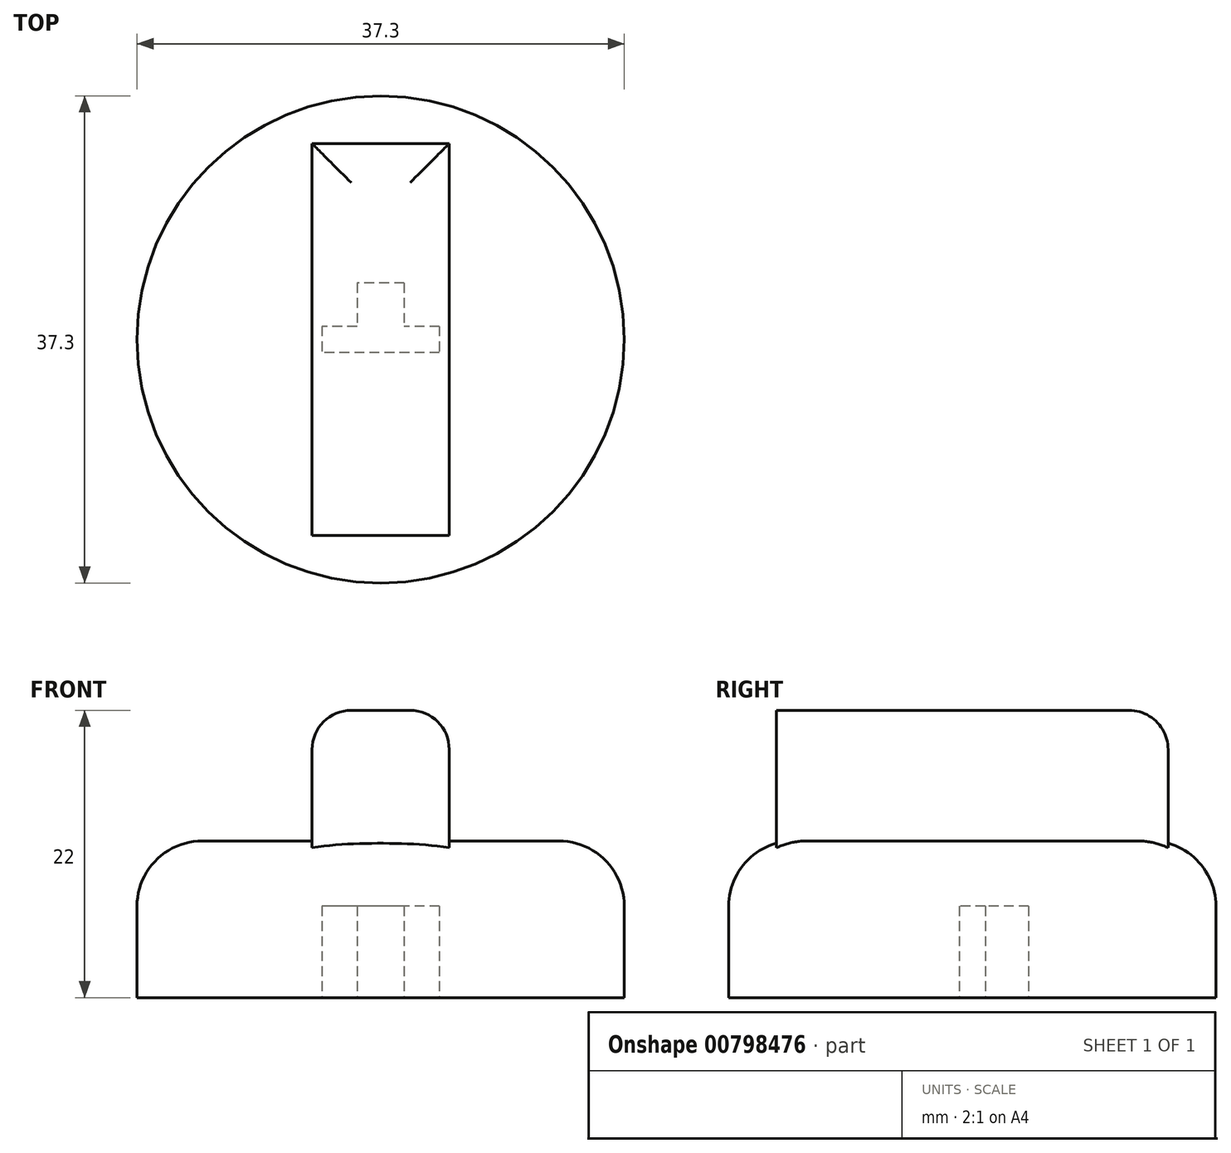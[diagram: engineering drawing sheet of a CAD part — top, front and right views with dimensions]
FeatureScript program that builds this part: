
annotation { "Feature Type Name" : "Feature", "Feature Type Description" : "" }
export const myFeature = defineFeature(function(context is Context, id is Id, definition is map)
    precondition{}
    {
        {
            var Q0;
            Q0=qCreatedBy(makeId("Top.planeOp"),FACE);
            var sketch = newSketch(context, id + "F0", { "sketchPlane" : qUnion([Q0])});
            skLineSegment(sketch, "E0.bottom", {"start": v(4.5, 1) * mm, "end": v(-4.5, 1) * mm});
            skLineSegment(sketch, "E0.top", {"start": v(4.5, -1) * mm, "end": v(-4.5, -1) * mm});
            skLineSegment(sketch, "E0.left", {"start": v(4.5, 1) * mm, "end": v(4.5, -1) * mm});
            skLineSegment(sketch, "E0.right", {"start": v(-4.5, 1) * mm, "end": v(-4.5, -1) * mm});
            skPoint(sketch, "E0.middle", {"position": v(0, 0) * mm});
            skLineSegment(sketch, "E1.bottom", {"start": v(1.8, 4.32) * mm, "end": v(-1.8, 4.32) * mm});
            skLineSegment(sketch, "E1.top", {"start": v(1.8, -1) * mm, "end": v(-1.8, -1) * mm});
            skLineSegment(sketch, "E1.left", {"start": v(1.8, 4.32) * mm, "end": v(1.8, -1) * mm});
            skLineSegment(sketch, "E1.right", {"start": v(-1.8, 4.32) * mm, "end": v(-1.8, -1) * mm});
            skPoint(sketch, "E1.middle", {"position": v(0, 1.66) * mm});
            skCircle(sketch, "E2", {"center": v(0, 0) * mm, "radius": 7 * mm});
            skCircle(sketch, "E3", {"center": v(0, 0) * mm, "radius": 18.65 * mm});
            skSolve(sketch);
        }
        {
            var Q0;
            {var subQ6=sQuery(id+"F0.wireOp",EDGE,"E0.left");Q0=makeQuery(id+"F0.imprint","IMPRINT",FACE,{"disambiguationData":[TD([[makeQuery(id+"F0.imprint","IMPRINT",EDGE,{"derivedFrom":subQ6}),1.0]])]});}
            var Q1;
            Q1=makeQuery(id+"F0.imprint","IMPRINT",FACE,{"disambiguationData":[TD([[makeQuery(id+"F0.imprint","IMPRINT",EDGE,{"derivedFrom":sQuery(id+"F0.wireOp",EDGE,"DuWAy8s3-9niQ-0Ztb-yx9R-YSX4JACFSrxY.bottom")}),-1.0]])]});
            var Q2;
            {var subQ0=sQuery(id+"F0.wireOp",EDGE,"R6NQIhES-pdkj-K8EB-Oj1V-QdIjAMpZzTrn.top");Q2=makeQuery(id+"F0.imprint","IMPRINT",FACE,{"disambiguationData":[TD([[makeQuery(id+"F0.imprint","IMPRINT",EDGE,{"derivedFrom":subQ0}),-1.0]])]});}
            extrude(context, id + "F1", {"entities" : qUnion([Q0, Q1, Q2]), "depth" : 12 * mm, "offsetDistance" : 25 * mm});
        }
        {
            var Q0;
            Q0=makeQuery(id+"F0.imprint","IMPRINT",FACE,{"disambiguationData":[TD([[makeQuery(id+"F0.imprint","IMPRINT",EDGE,{"derivedFrom":sQuery(id+"F0.wireOp",EDGE,"E2")}),-1.0]])]});
            extrude(context, id + "F2", {"entities" : qUnion([Q0]), "operationType" : NewBodyOperationType.ADD, "depth" : 12 * mm, "offsetDistance" : 25 * mm});
        }
        {
            var Q0;
            Q0=makeQuery(id+"F2.opExtrude","CAP_EDGE",EDGE,{"disambiguationData":[OSD([sQuery(id+"F0.wireOp",EDGE,"E3")])],"isStart":false});
            fillet(context, id + "F3", {"entities" : qUnion([Q0]), "radius" : 5 * mm, "tangentPropagation" : true, "allowEdgeOverflow" : false});
        }
        {
            var Q0;
            Q0=qCreatedBy(makeId("Top.planeOp"),FACE);
            cPlane(context, id + "F4", {"entities" : qUnion([Q0]), "cplaneType" : CPlaneType.OFFSET, "offset" : 7 * mm, "width" : 150 * mm, "height" : 150 * mm});
        }
        {
            var Q0;
            Q0=qCreatedBy(id+"F4.planeOp",FACE);
            var sketch = newSketch(context, id + "F5", { "sketchPlane" : qUnion([Q0])});
            skLineSegment(sketch, "E4.bottom", {"start": v(5.25, 15) * mm, "end": v(-5.25, 15) * mm});
            skLineSegment(sketch, "E4.top", {"start": v(5.25, -15) * mm, "end": v(-5.25, -15) * mm});
            skLineSegment(sketch, "E4.left", {"start": v(5.25, 15) * mm, "end": v(5.25, -15) * mm});
            skLineSegment(sketch, "E4.right", {"start": v(-5.25, 15) * mm, "end": v(-5.25, -15) * mm});
            skPoint(sketch, "E4.middle", {"position": v(0, 0) * mm});
            skSolve(sketch);
        }
        {
            var Q0;
            Q0 = qSketchRegion(id + "F5", true);
            extrude(context, id + "F6", {"entities" : qUnion([Q0]), "operationType" : NewBodyOperationType.ADD, "depth" : 15 * mm, "offsetDistance" : 25 * mm});
        }
        {
            var Q0;
            Q0=makeQuery(id+"F6.opExtrude","CAP_EDGE",EDGE,{"disambiguationData":[OSD([sQuery(id+"F5.wireOp",EDGE,"E4.bottom")])],"isStart":false});
            var Q1;
            Q1=makeQuery(id+"F6.opExtrude","CAP_EDGE",EDGE,{"disambiguationData":[OSD([sQuery(id+"F5.wireOp",EDGE,"E4.right")])],"isStart":false});
            var Q2;
            Q2=makeQuery(id+"F6.opExtrude","CAP_EDGE",EDGE,{"disambiguationData":[OSD([sQuery(id+"F5.wireOp",EDGE,"E4.left")])],"isStart":false});
            fillet(context, id + "F7", {"entities" : qUnion([Q0, Q1, Q2]), "radius" : 3 * mm, "tangentPropagation" : true, "allowEdgeOverflow" : false});
        }
    });
